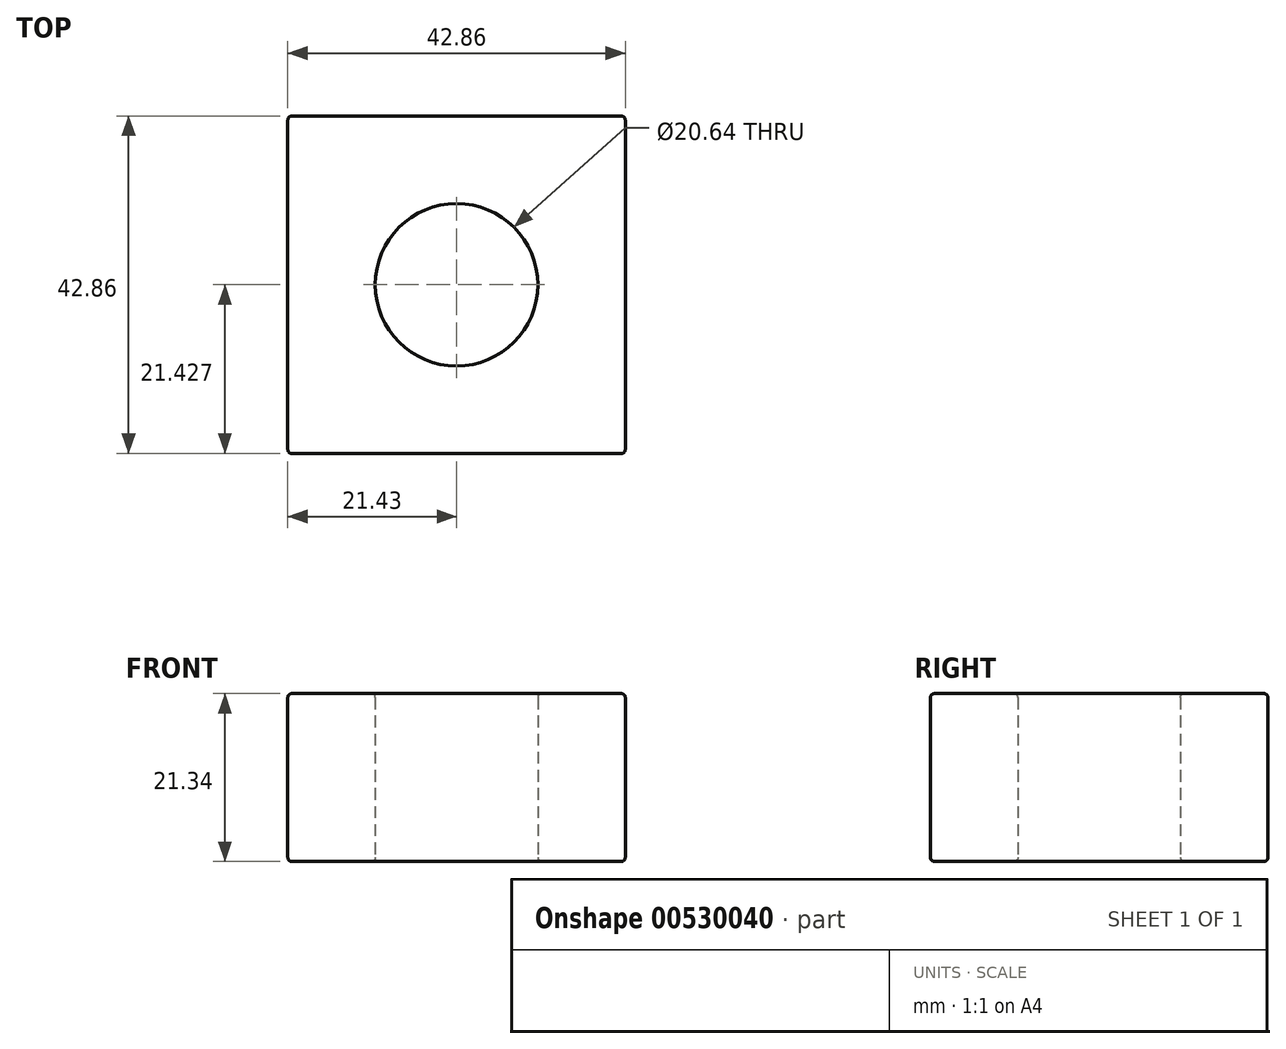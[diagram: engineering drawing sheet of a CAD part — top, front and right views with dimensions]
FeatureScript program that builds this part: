
annotation { "Feature Type Name" : "Feature", "Feature Type Description" : "" }
export const myFeature = defineFeature(function(context is Context, id is Id, definition is map)
    precondition{}
    {
        {
            var Q0;
            Q0=qCreatedBy(makeId("Top.planeOp"),FACE);
            var sketch = newSketch(context, id + "F0", { "sketchPlane" : qUnion([Q0])});
            skLineSegment(sketch, "E0.bottom", {"start": v(6.82, -5.16) * mm, "end": v(49.68, -5.16) * mm});
            skLineSegment(sketch, "E0.top", {"start": v(6.82, -48.02) * mm, "end": v(49.68, -48.02) * mm});
            skLineSegment(sketch, "E0.left", {"start": v(6.82, -5.16) * mm, "end": v(6.82, -48.02) * mm});
            skLineSegment(sketch, "E0.right", {"start": v(49.68, -5.16) * mm, "end": v(49.68, -48.02) * mm});
            skLineSegment(sketch, "E1", {"start": v(28.25, -5.16) * mm, "end": v(28.25, -48.02) * mm, "construction": true});
            skCircle(sketch, "E2", {"center": v(28.25, -26.6) * mm, "radius": 10.32 * mm});
            skSolve(sketch);
        }
        {
            var Q0;
            Q0=qSketchRegion(id+"F0",true);
            extrude(context, id + "F1", {"entities" : qUnion([Q0]), "depth" : 21.34 * mm});
        }
        {
            var Q0;
            Q0=makeQuery(id+"F1.opExtrude","CAP_EDGE",EDGE,{"disambiguationData":[OSD([sQuery(id+"F0.wireOp",EDGE,"E0.bottom")])],"isStart":true});
            var Q1;
            Q1=makeQuery(id+"F1.opExtrude","SWEPT_EDGE",EDGE,{"disambiguationData":[OSD([sQuery(id+"F0.wireOp",EDGE,"E0.bottom"),sQuery(id+"F0.wireOp",EDGE,"E0.left")])]});
            var Q2;
            Q2=makeQuery(id+"F1.opExtrude","CAP_EDGE",EDGE,{"disambiguationData":[OSD([sQuery(id+"F0.wireOp",EDGE,"E0.bottom")])],"isStart":false});
            var Q3;
            Q3=makeQuery(id+"F1.opExtrude","SWEPT_FACE",FACE,{"disambiguationData":[OSD([sQuery(id+"F0.wireOp",EDGE,"E0.bottom")])]});
            var Q4;
            Q4=makeQuery(id+"F1.opExtrude","CAP_FACE",FACE,{"disambiguationData":[OSD([sQuery(id+"F0.wireOp",EDGE,"E0.bottom"),sQuery(id+"F0.wireOp",EDGE,"E0.top"),sQuery(id+"F0.wireOp",EDGE,"E0.left"),sQuery(id+"F0.wireOp",EDGE,"E0.right"),sQuery(id+"F0.wireOp",EDGE,"E2")])],"isStart":true});
            var Q5;
            Q5=makeQuery(id+"F1.opExtrude","SWEPT_FACE",FACE,{"disambiguationData":[OSD([sQuery(id+"F0.wireOp",EDGE,"E0.right")])]});
            var Q6;
            Q6=makeQuery(id+"F1.opExtrude","CAP_FACE",FACE,{"disambiguationData":[OSD([sQuery(id+"F0.wireOp",EDGE,"E0.bottom"),sQuery(id+"F0.wireOp",EDGE,"E0.top"),sQuery(id+"F0.wireOp",EDGE,"E0.left"),sQuery(id+"F0.wireOp",EDGE,"E0.right"),sQuery(id+"F0.wireOp",EDGE,"E2")])],"isStart":false});
            var Q7;
            Q7=makeQuery(id+"F1.opExtrude","SWEPT_EDGE",EDGE,{"disambiguationData":[OSD([sQuery(id+"F0.wireOp",EDGE,"E0.top"),sQuery(id+"F0.wireOp",EDGE,"E0.left")])]});
            fillet(context, id + "F2", {"entities" : qUnion([Q0, Q1, Q2, Q3, Q4, Q5, Q6, Q7]), "radius" : 0.5 * mm, "tangentPropagation" : true, "allowEdgeOverflow" : false});
        }
    });
